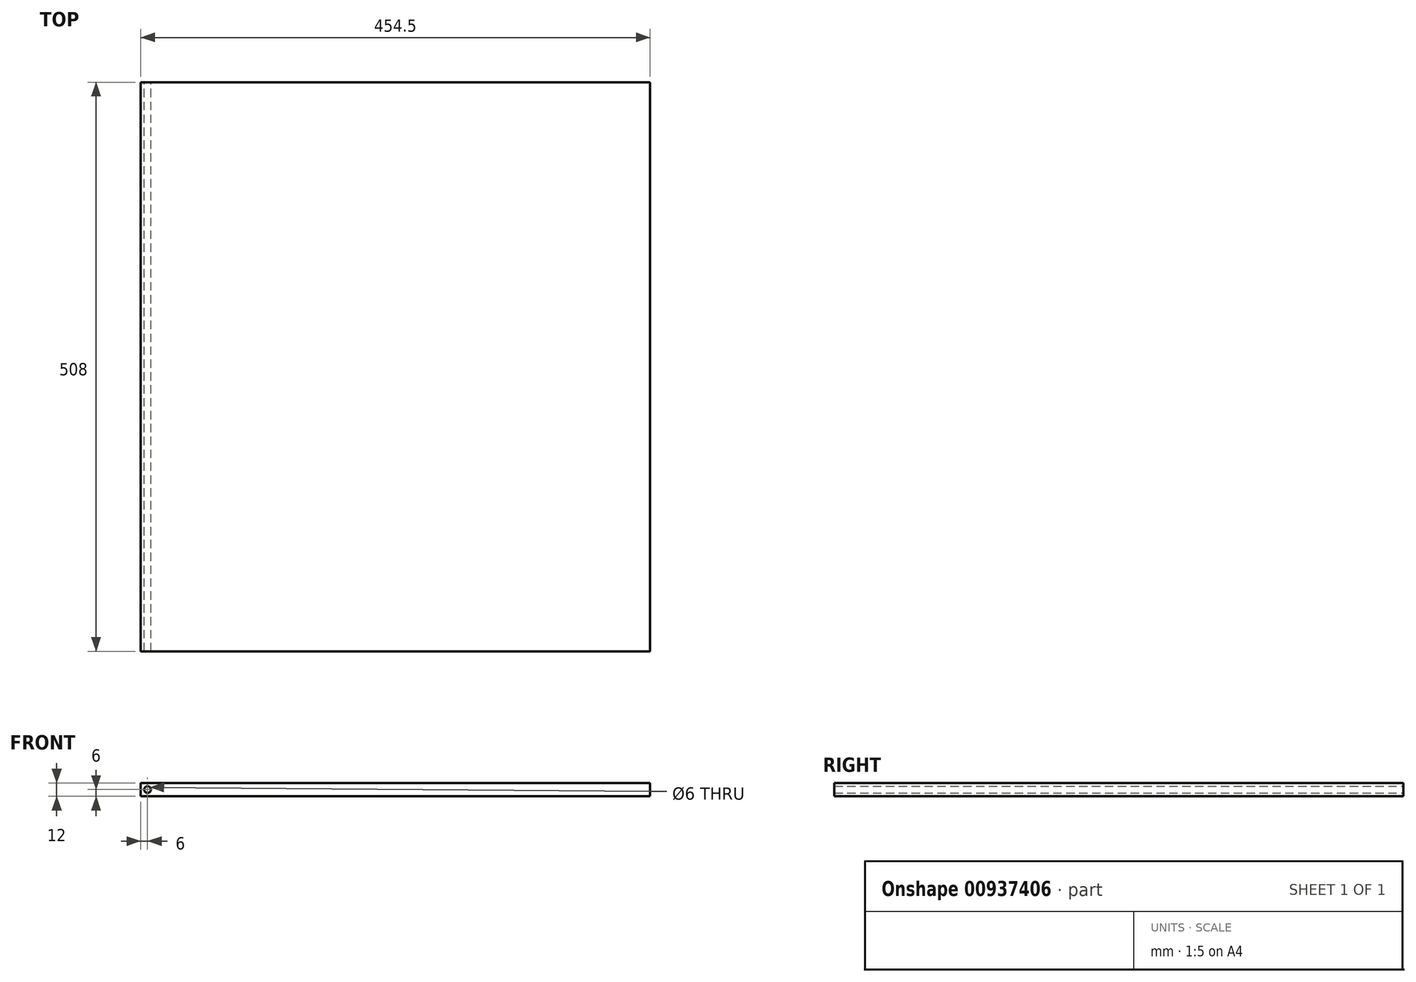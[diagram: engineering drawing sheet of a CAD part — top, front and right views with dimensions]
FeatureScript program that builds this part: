
annotation { "Feature Type Name" : "Feature", "Feature Type Description" : "" }
export const myFeature = defineFeature(function(context is Context, id is Id, definition is map)
    precondition{}
    {
        {
            var Q0;
            Q0=qCreatedBy(makeId("Front.planeOp"),FACE);
            var sketch = newSketch(context, id + "F0", { "sketchPlane" : qUnion([Q0])});
            skLineSegment(sketch, "E0.bottom", {"start": v(0, 0) * mm, "end": v(454.5, 0) * mm});
            skLineSegment(sketch, "E0.top", {"start": v(0, -12) * mm, "end": v(454.5, -12) * mm});
            skLineSegment(sketch, "E0.left", {"start": v(0, 0) * mm, "end": v(0, -12) * mm});
            skLineSegment(sketch, "E0.right", {"start": v(454.5, 0) * mm, "end": v(454.5, -12) * mm});
            skPoint(sketch, "E1.orphan", {"position": v(454.5, -6) * mm});
            skCircle(sketch, "E2", {"center": v(6, -6) * mm, "radius": 3 * mm});
            skPoint(sketch, "E3.start.orphan", {"position": v(0, -6) * mm});
            skSolve(sketch);
        }
        {
            var Q0;
            Q0 = qSketchRegion(id + "F0", true);
            extrude(context, id + "F1", {"entities" : qUnion([Q0]), "depth" : 508 * mm, "offsetDistance" : 25.4 * mm});
        }
    });
